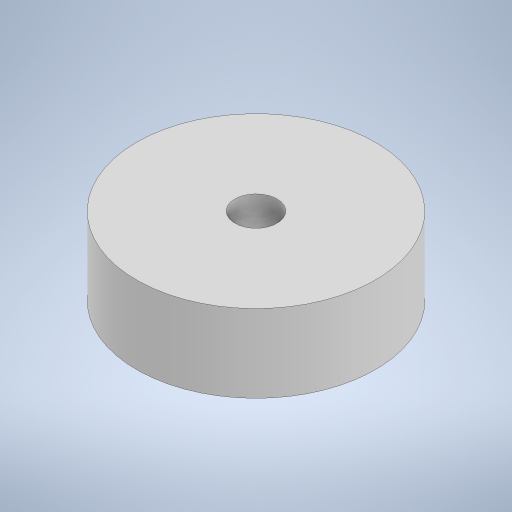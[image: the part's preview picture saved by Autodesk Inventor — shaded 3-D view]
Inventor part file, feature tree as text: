
AUTODESK INVENTOR PART (.ipt)
format: ipt  version: 2024.1 (Build 281209000, 209)  size: 201,216 bytes
history: native  units: mm
features: other x1, extrude x1, sketch x1
ambient origin geometry x8: Origin, YZ Plane, XZ Plane, XY Plane, X Axis, Y Axis, Z Axis, Center Point
bodies: Body1 (feature_tree)
feature tree (3):
  other  "ソリッド1"
  extrude  "押し出し1"  Depth=21.5mm
  sketch  "スケッチ1"
